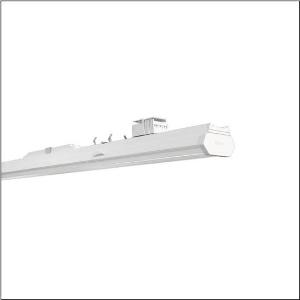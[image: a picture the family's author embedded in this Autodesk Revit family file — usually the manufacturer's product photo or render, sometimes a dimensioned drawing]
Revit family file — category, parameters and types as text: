
# Revit family: licross_r__11_protected_ho_51tp12dn4fxm3s_598f
name_source: partatom
category: Lighting Fixtures
units: mm (PartAtom-declared; Revit-internal decimal feet)

## family parameters
Cut with Voids When Loaded = No
Host = Face
Light Source = No
Part Type = Normal
Room Calculation Point = No
Round Connector Dimension = Use Diameter
Shared = No

## types (1)
- --- (1 x LED, 970 lm, 7.4 W, 4000K)
    Apparent Load = 7 VA
    CIE Flux Codes = 70 91 97 98 100
    Color Rendering = 80
    Color Temperature = 4000K
    Default Elevation = 1800 mm
    Description = Licross® 11 Protected HO, luminaire insert, of sheet steel, galvanised, coil coated, white, length: 1.500mm, width: 90mm, height: 101mm, LED rated luminous flux: 15.270lm, light colour: 840, SDCM (Standard Deviation of Colour Matching)MacAdam ≤ 2 SDCM (initial), control gear: DALI 2 (for two DALI lines), with plug, 6-pole, with phase selection, for trunking rail, 14-core, mains connection: 220..240V, AC, 50/60Hz, rated input power: 91W, for trunking rail, 14-core, internal wiring halogen-free, for emergency light function, converter,control gear: single battery element, battery: LiFePO4, 9Ah, primary light control with lens, of plastic, primary optical cover: cover, of PMMA, light emission: direct distribution, primary light characteristic: symmetric, protection rating (complete): IP64, insulation class (complete): insulation class I (protective earthing), certification: CE, UKCA, protection symbol: D if used in an environment with conductive dust loads with corresponding accessories, impact resistance: IK06, permissible ambient temperature for indoor applications: +5..+30°C, standard: EN 60598-2-22, LABS conformity tested according to VDMA 24364:2018-05, reducing of maximum allowable ambient temperature of 5°C with ceiling mounting, corresponds to IFS (International Featured Standards) requirements for safety and quality in the food industry, packaging unit: 1 piece
    Height = 92 mm
    Lamp = 1 x LED
    Lamp Light Flux = 970 lm
    Lamp Power = 7.4 W
    Lamp count = 1
    Length = 1500 mm
    Luminous efficacy = 131 lm/W
    Manufacturer = Siteco
    ModVariant = No
    Model = 51TP12DN4FXM3S
    Mounting Place = Ceiling
    Mounting Type = Pendant
    Number of Poles = 1
    OnlyDefault = Yes
    Power Factor = 1
    Product Name = Licross® 11 Protected HO
    Product group = luminaire insert | ceiling pendant
    ProductGroupID = 901
    Protection Class = Protection class I
    Protection Degree = IP 64
    RLX_Detail_Level = 1
    RLX_Emergency_Light_Flux = 0 lm
    RLX_Emergency_Type = 0
    RLX_Emergency_Type_DB = No
    RlxData = <blob elided: 25077 chars, md5=8960d6e6>
    Socket = socket
    Standby Power = 0 W
    System Light Flux = 970 lm
    System Power = 7 W
    Type Comments = : emergency light operation: 3 h
    Type Image = l_1256148.jpg
    URL = http://relux.com
    VarID = @adj_098791
    Voltage = 0 V
    Weight = 0.00 kg
    Width = 88 mm

## geometry (parser evidence)
native form markers: Blend x4, Sweep x9
no freeform markers — native parametric forms only
